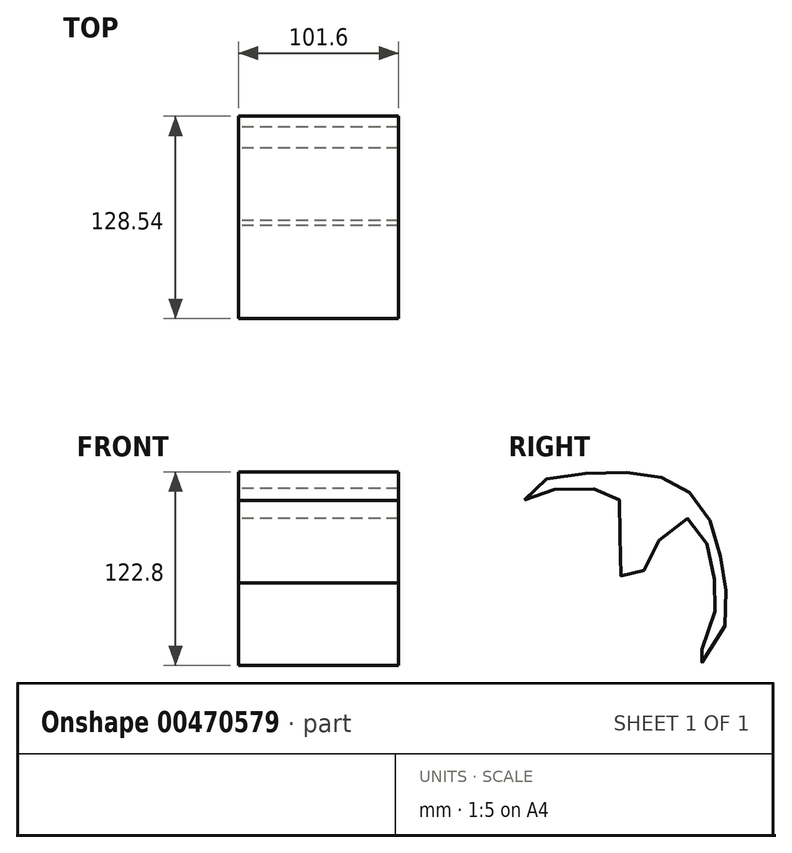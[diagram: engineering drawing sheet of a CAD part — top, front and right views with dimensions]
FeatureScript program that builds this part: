
annotation { "Feature Type Name" : "Feature", "Feature Type Description" : "" }
export const myFeature = defineFeature(function(context is Context, id is Id, definition is map)
    precondition{}
    {
        {
            var Q0;
            Q0=qCreatedBy(makeId("Right.planeOp"),FACE);
            var sketch = newSketch(context, id + "F0", { "sketchPlane" : qUnion([Q0])});
            skFitSpline(sketch, "E0", {"points": [v(-76.13, 49.56) * mm, v(-62.92, 55.02) * mm, v(-35.62, 56.74) * mm, v(-19.25, 54.15) * mm, v(-14.08, 38.93) * mm, v(-17.24, 12.2) * mm, v(-10.34, -3.02) * mm, v(4.3, 12.78) * mm, v(10.92, 26.57) * mm, v(29.3, 37.78) * mm, v(39.65, 21.98) * mm, v(44.24, 0) * mm, v(45.1, -17.1) * mm, v(38.78, -40.94) * mm, v(32.18, -55.3) * mm, v(46.54, -42.38) * mm, v(52.29, -14.8) * mm, v(50.85, 0) * mm, v(45.68, 25.14) * mm, v(37.63, 43.52) * mm, v(23.27, 58.46) * mm, v(7.76, 64.78) * mm, v(-14.36, 67.37) * mm, v(-43.1, 66.22) * mm, v(-66.94, 60.47) * mm, v(-76.13, 49.56) * mm]});
            skSolve(sketch);
        }
        {
            var Q0;
            Q0 = qSketchRegion(id + "F0", true);
            extrude(context, id + "F1", {"entities" : qUnion([Q0]), "depth" : 101.6 * mm});
        }
    });
